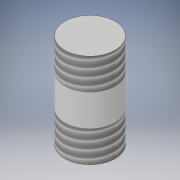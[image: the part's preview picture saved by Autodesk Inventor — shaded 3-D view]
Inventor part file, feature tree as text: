
AUTODESK INVENTOR PART (.ipt)
format: ipt  version: 2019 (Build 230136000, 136)  size: 104,448 bytes
history: native  units: mm
features: thread x2, revolve x1, sketch x1
ambient origin geometry x8: Origin, YZ Plane, XZ Plane, XY Plane, X Axis, Y Axis, Z Axis, Center Point
bodies: Solid1 (feature_tree)
feature tree (4):
  revolve  "Revolution1"  [1 undecoded]
  thread  "Thread1"  [1 undecoded]
  thread  "Thread2"  [1 undecoded]
  sketch  "Sketch1"  dims[d0=8.0mm d1=15.0mm d2=90.0deg d3=5.0mm d4=0.0mm d5=5.0mm d6=0.0mm]
note: 3 required parameter values undecoded (feature->parameter linkage not recoverable at this tier; creation-order binding heuristic only, values carry confidence <= 0.55)